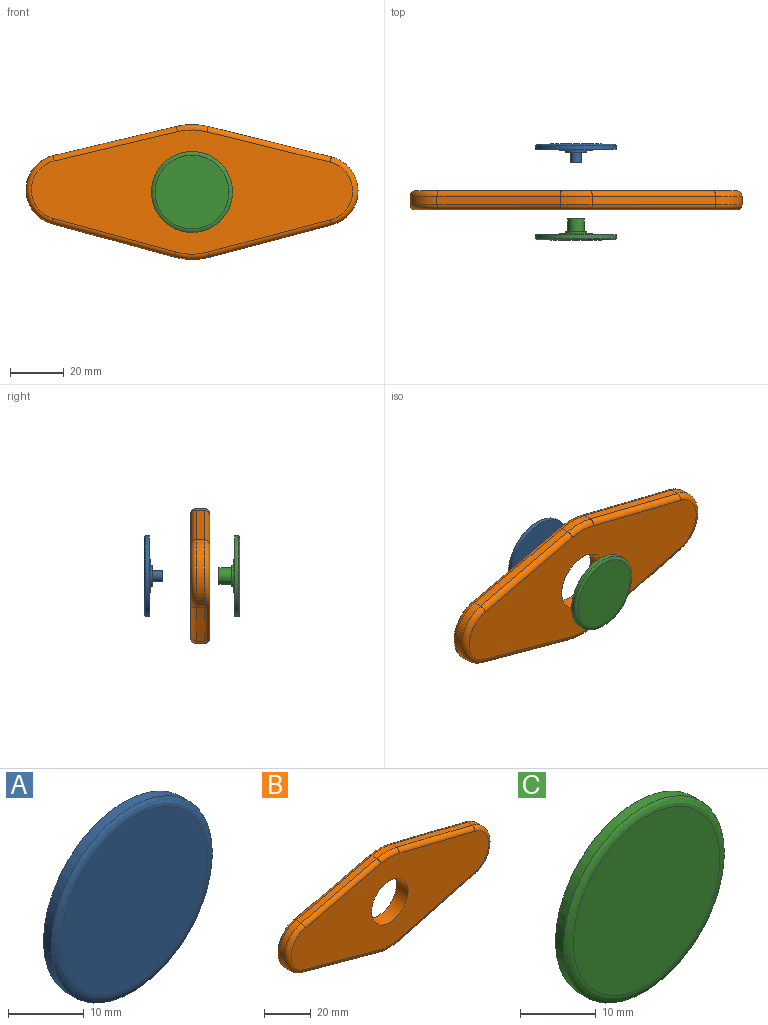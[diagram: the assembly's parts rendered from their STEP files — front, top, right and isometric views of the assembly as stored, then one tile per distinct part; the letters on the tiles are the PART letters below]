
ASSEMBLY  parts=3 mates=3
PART A: 11 faces, bbox 32.7x7x32.7 mm
  f0: cylinder r=15mm len=30mm, axis (0,1,0), area 141.4mm2, adj f2,f9
  f1: plane 27.35x27.35mm, normal (0,-1,0), area 587.7mm2, adj f9
  f2: plane 30x30mm, normal (0,1,0), area 593.8mm2, adj f0,f3
  f3: cylinder r=6mm len=12mm, axis (0,-1,0), area 18.8mm2, adj f2,f4
  f4: plane 12x12mm, normal (0,1,0), area 62.8mm2, adj f3,f5
  f5: cylinder r=4mm len=8mm, axis (0,-1,0), area 12.6mm2, adj f4,f6
  f6: plane 8x8mm, normal (0,1,0), area 37.7mm2, adj f5,f7
  f7: cylinder r=2mm len=4mm, axis (0,-1,0), area 47.8mm2, adj f6,f10
  f8: plane 3.6x3.6mm, normal (0,1,0), area 10.2mm2, adj f10
  f9: torus R=13.68mm, axis (0,1,0), area 130.5mm2, adj f0,f1
  f10: cone r=2mm half-angle=45deg, axis (0,-1,0), area 3.4mm2, adj f7,f8
PART B: 27 faces, bbox 125.1x7x54.1 mm
  f0: cylinder r=13mm len=25.19mm, axis (0,1,0), area 103mm2, adj f1,f7,f16,f20
  f1: plane 45.34x12.39mm, normal (-0.26,0,-0.96), area 141mm2, adj f0,f2,f18,f22
  f2: cylinder r=25mm len=12.96mm, axis (0,1,0), area 39.3mm2, adj f1,f3,f17,f24
  f3: plane 45.45x11.97mm, normal (0.25,0,-0.97), area 141mm2, adj f2,f4,f15,f26
  f4: cylinder r=13mm len=25.19mm, axis (0,1,0), area 103mm2, adj f3,f5,f13,f25
  f5: plane 45.63x11.28mm, normal (0.24,0,0.97), area 141mm2, adj f4,f6,f11,f23
  f6: cylinder r=25mm len=11.78mm, axis (0,1,0), area 35.7mm2, adj f5,f7,f12,f21
  f7: plane 45.73x10.86mm, normal (-0.23,0,0.97), area 141mm2, adj f0,f6,f14,f19
  f8: cylinder r=11mm len=22mm, axis (0,1,0), area 483.8mm2, adj f9,f10
  f9: plane 119.01x46mm, normal (0,-1,0), area 3400mm2, adj f8,f19,f20,f21,f22,f23,f24,f25
  f10: plane 119.01x46mm, normal (0,1,0), area 3400mm2, adj f8,f11,f12,f13,f14,f15,f16,f17
  f11: cylinder r=2mm len=46.11mm, axis (-0.97,0,0.24), area 147.7mm2, adj f5,f10,f12,f13
  f12: torus R=23mm, axis (0,-1,0), area 36.3mm2, adj f6,f10,f11,f14
  f13: torus R=11mm, axis (0,-1,0), area 101.9mm2, adj f4,f10,f11,f15
  f14: cylinder r=2mm len=46.19mm, axis (-0.97,0,-0.23), area 147.7mm2, adj f7,f10,f12,f16
  f15: cylinder r=2mm len=45.96mm, axis (0.97,0,0.25), area 147.7mm2, adj f3,f10,f13,f17
  f16: torus R=11mm, axis (0,-1,0), area 101.9mm2, adj f0,f10,f14,f18
  f17: torus R=23mm, axis (0,-1,0), area 40mm2, adj f2,f10,f15,f18
  f18: cylinder r=2mm len=45.87mm, axis (0.96,0,-0.26), area 147.7mm2, adj f1,f10,f16,f17
  f19: cylinder r=2mm len=46.19mm, axis (0.97,0,0.23), area 147.7mm2, adj f7,f9,f20,f21
  f20: torus R=11mm, axis (0,-1,0), area 101.9mm2, adj f0,f9,f19,f22
  f21: torus R=23mm, axis (0,-1,0), area 36.3mm2, adj f6,f9,f19,f23
  f22: cylinder r=2mm len=45.87mm, axis (-0.96,0,0.26), area 147.7mm2, adj f1,f9,f20,f24
  f23: cylinder r=2mm len=46.11mm, axis (0.97,0,-0.24), area 147.7mm2, adj f5,f9,f21,f25
  f24: torus R=23mm, axis (0,-1,0), area 40mm2, adj f2,f9,f22,f26
  f25: torus R=11mm, axis (0,-1,0), area 101.9mm2, adj f4,f9,f23,f26
  f26: cylinder r=2mm len=45.96mm, axis (-0.97,0,-0.25), area 147.7mm2, adj f3,f9,f24,f25
PART C: 13 faces, bbox 32.7x8x32.7 mm
  f0: cylinder r=15mm len=30mm, axis (0,1,0), area 141.4mm2, adj f2,f7
  f1: plane 27.35x27.35mm, normal (0,-1,0), area 587.7mm2, adj f7
  f2: plane 30x30mm, normal (0,1,0), area 593.8mm2, adj f0,f3
  f3: cylinder r=6mm len=12mm, axis (0,-1,0), area 18.8mm2, adj f2,f4
  f4: plane 12x12mm, normal (0,1,0), area 62.8mm2, adj f3,f5
  f5: cylinder r=4mm len=8mm, axis (0,-1,0), area 12.6mm2, adj f4,f6
  f6: plane 8x8mm, normal (0,1,0), area 22mm2, adj f5,f8
  f7: torus R=13.68mm, axis (0,1,0), area 130.5mm2, adj f0,f1
  f8: cylinder r=3mm len=6mm, axis (0,-1,0), area 90.5mm2, adj f6,f12
  f9: plane 5.6x5.6mm, normal (0,1,0), area 12.1mm2, adj f11,f12
  f10: plane 4x4mm, normal (0,1,0), area 12.6mm2, adj f11
  f11: cylinder r=2mm len=5.5mm, axis (0,-1,0), area 69.1mm2, adj f9,f10
  f12: cone r=2.8mm half-angle=45deg, axis (0,-1,0), area 5.2mm2, adj f8,f9
PLACE A rot(axis=(1,0,-0.01),180deg) t=(0,15.33,0)mm
PLACE B at identity fixed
PLACE C rot(axis=(0,1,0),0.8deg) t=(0,-16.21,0)mm
MATE slider A.f0 <-> C.f0  axis (0,-1,0) through (0,10.33,0)mm
MATE cylindrical C.f0 <-> B.f2  axis (0,-1,0) through (0,-18.21,0)mm
MATE cylindrical A.f0 <-> B.f2  axis (0,1,0) through (0,17.33,0)mm
